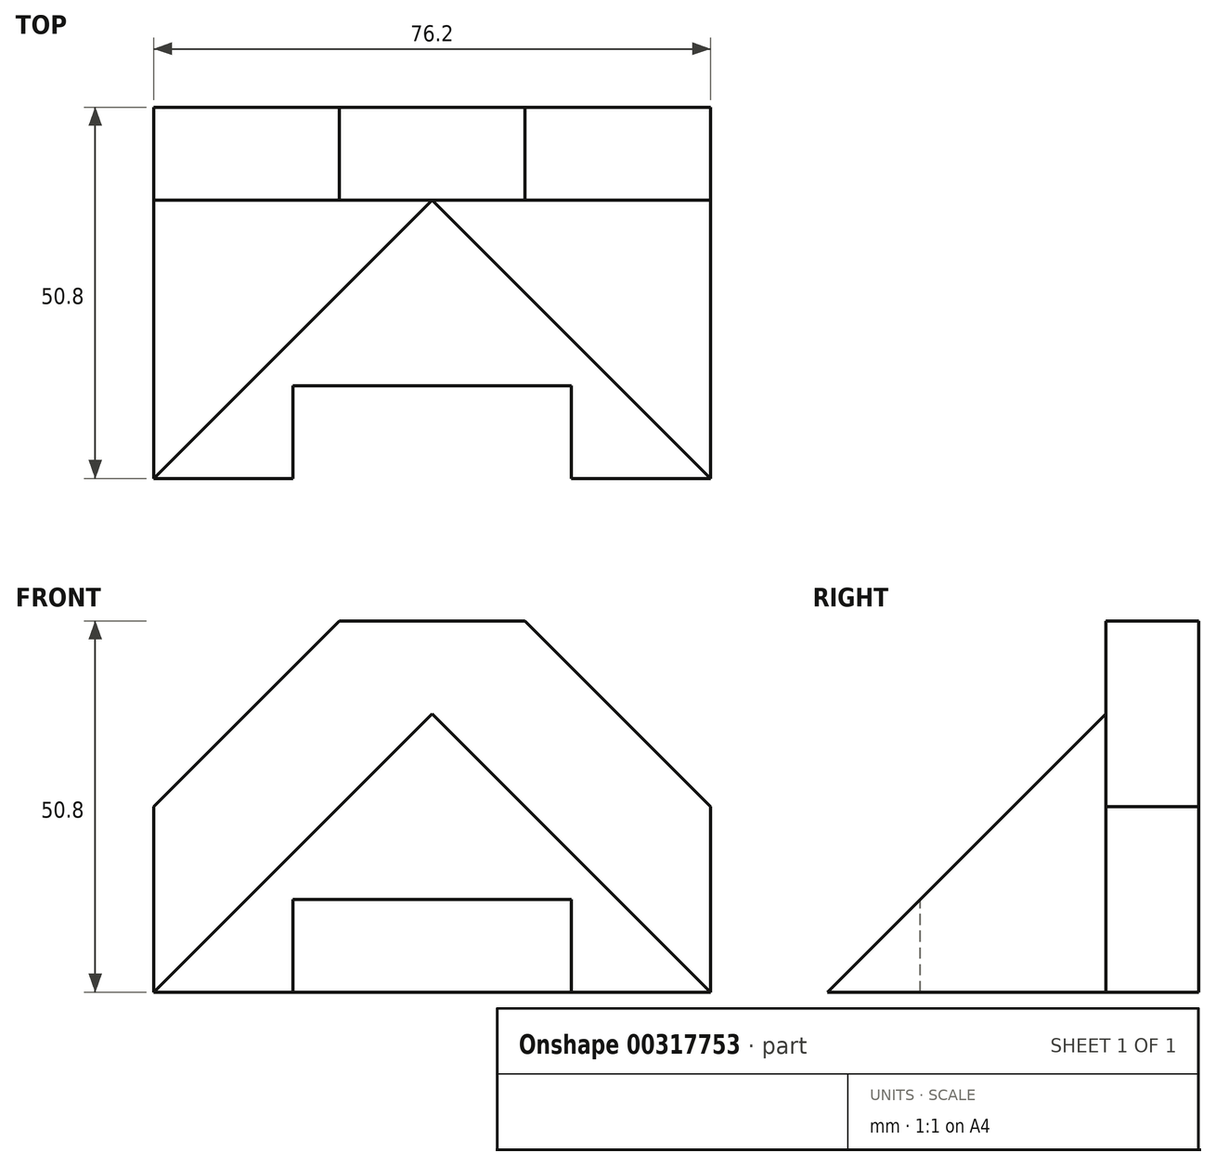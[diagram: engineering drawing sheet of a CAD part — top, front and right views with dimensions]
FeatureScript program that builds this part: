
annotation { "Feature Type Name" : "Feature", "Feature Type Description" : "" }
export const myFeature = defineFeature(function(context is Context, id is Id, definition is map)
    precondition{}
    {
        {
            var Q0;
            Q0=qCreatedBy(makeId("Top.planeOp"),FACE);
            var sketch = newSketch(context, id + "F0", { "sketchPlane" : qUnion([Q0])});
            skLineSegment(sketch, "E0.bottom", {"start": v(0, 0) * mm, "end": v(76.2, 0) * mm});
            skLineSegment(sketch, "E0.top", {"start": v(0, 50.8) * mm, "end": v(76.2, 50.8) * mm});
            skLineSegment(sketch, "E0.left", {"start": v(0, 0) * mm, "end": v(0, 50.8) * mm});
            skLineSegment(sketch, "E0.right", {"start": v(76.2, 0) * mm, "end": v(76.2, 50.8) * mm});
            skSolve(sketch);
        }
        {
            var Q0;
            Q0 = qSketchRegion(id + "F0", true);
            extrude(context, id + "F1", {"entities" : qUnion([Q0]), "depth" : 50.8 * mm});
        }
        {
            var Q0;
            Q0=makeQuery(id+"F1.opExtrude","SWEPT_FACE",FACE,{"disambiguationData":[OSD([sQuery(id+"F0.wireOp",EDGE,"E0.bottom")])]});
            var sketch = newSketch(context, id + "F2", { "sketchPlane" : qUnion([Q0])});
            skLineSegment(sketch, "E1", {"start": v(0, 0) * mm, "end": v(76.2, 0) * mm});
            skLineSegment(sketch, "E2", {"start": v(76.2, 0) * mm, "end": v(38.1, 38.1) * mm});
            skLineSegment(sketch, "E3", {"start": v(38.1, 38.1) * mm, "end": v(0, 0) * mm});
            skSolve(sketch);
        }
        {
            var Q0;
            Q0=makeQuery(id+"F2.imprint","IMPRINT",FACE,{"disambiguationData":[TD([[makeQuery(id+"F2.imprint","IMPRINT",EDGE,{"derivedFrom":sQuery(id+"F2.wireOp",EDGE,"E2")}),-1.0]])]});
            extrude(context, id + "F3", {"entities" : qUnion([Q0]), "operationType" : NewBodyOperationType.REMOVE, "oppositeDirection" : true, "depth" : 38.1 * mm});
        }
        {
            var Q0;
            Q0=makeQuery(id+"F3.boolean.opBoolean","COPY",FACE,{"derivedFrom":makeQuery(id+"F3.opExtrude","CAP_FACE",FACE,{"disambiguationData":[OSD([sQuery(id+"F0.wireOp",EDGE,"E0.bottom"),sQuery(id+"F0.wireOp",EDGE,"E0.left"),sQuery(id+"F0.wireOp",EDGE,"E0.right"),sQuery(id+"F2.wireOp",EDGE,"E2"),sQuery(id+"F2.wireOp",EDGE,"E3")])],"isStart":false})});
            var sketch = newSketch(context, id + "F4", { "sketchPlane" : qUnion([Q0])});
            skLineSegment(sketch, "E4", {"start": v(0, 50.8) * mm, "end": v(0, 25.4) * mm});
            skLineSegment(sketch, "E5", {"start": v(0, 25.4) * mm, "end": v(25.4, 50.8) * mm});
            skLineSegment(sketch, "E6", {"start": v(25.4, 50.8) * mm, "end": v(0, 50.8) * mm});
            skLineSegment(sketch, "E7", {"start": v(76.2, 50.8) * mm, "end": v(76.2, 25.4) * mm});
            skLineSegment(sketch, "E8", {"start": v(76.2, 25.4) * mm, "end": v(50.8, 50.8) * mm});
            skLineSegment(sketch, "E9", {"start": v(50.8, 50.8) * mm, "end": v(76.2, 50.8) * mm});
            skSolve(sketch);
        }
        {
            var Q0;
            Q0 = qSketchRegion(id + "F4", true);
            extrude(context, id + "F5", {"entities" : qUnion([Q0]), "operationType" : NewBodyOperationType.REMOVE, "endBound" : BoundingType.THROUGH_ALL, "oppositeDirection" : true, "depth" : 25.4 * mm});
        }
        {
            var Q0;
            Q0=makeQuery(id+"F1.opExtrude","SWEPT_FACE",FACE,{"disambiguationData":[OSD([sQuery(id+"F0.wireOp",EDGE,"E0.right")])]});
            var sketch = newSketch(context, id + "F6", { "sketchPlane" : qUnion([Q0])});
            skLineSegment(sketch, "E10", {"start": v(0, 0) * mm, "end": v(0, 38.1) * mm});
            skLineSegment(sketch, "E11", {"start": v(0, 38.1) * mm, "end": v(38.1, 38.1) * mm});
            skLineSegment(sketch, "E12", {"start": v(38.1, 38.1) * mm, "end": v(0, 0) * mm});
            skSolve(sketch);
        }
        {
            var Q0;
            Q0 = qSketchRegion(id + "F6", true);
            extrude(context, id + "F7", {"entities" : qUnion([Q0]), "operationType" : NewBodyOperationType.REMOVE, "endBound" : BoundingType.THROUGH_ALL, "oppositeDirection" : true, "depth" : 25.4 * mm});
        }
        {
            var Q0;
            Q0=makeQuery(id+"F1.opExtrude","CAP_FACE",FACE,{"disambiguationData":[OSD([sQuery(id+"F0.wireOp",EDGE,"E0.bottom"),sQuery(id+"F0.wireOp",EDGE,"E0.top"),sQuery(id+"F0.wireOp",EDGE,"E0.left"),sQuery(id+"F0.wireOp",EDGE,"E0.right")])],"isStart":false});
            var sketch = newSketch(context, id + "F8", { "sketchPlane" : qUnion([Q0])});
            skLineSegment(sketch, "E13.bottom", {"start": v(19.05, 0) * mm, "end": v(57.15, 0) * mm});
            skLineSegment(sketch, "E13.top", {"start": v(19.05, 12.7) * mm, "end": v(57.15, 12.7) * mm});
            skLineSegment(sketch, "E13.left", {"start": v(19.05, 0) * mm, "end": v(19.05, 12.7) * mm});
            skLineSegment(sketch, "E13.right", {"start": v(57.15, 0) * mm, "end": v(57.15, 12.7) * mm});
            skSolve(sketch);
        }
        {
            var Q0;
            Q0 = qSketchRegion(id + "F8", true);
            extrude(context, id + "F9", {"entities" : qUnion([Q0]), "operationType" : NewBodyOperationType.REMOVE, "endBound" : BoundingType.THROUGH_ALL, "oppositeDirection" : true, "depth" : 25.4 * mm});
        }
    });
